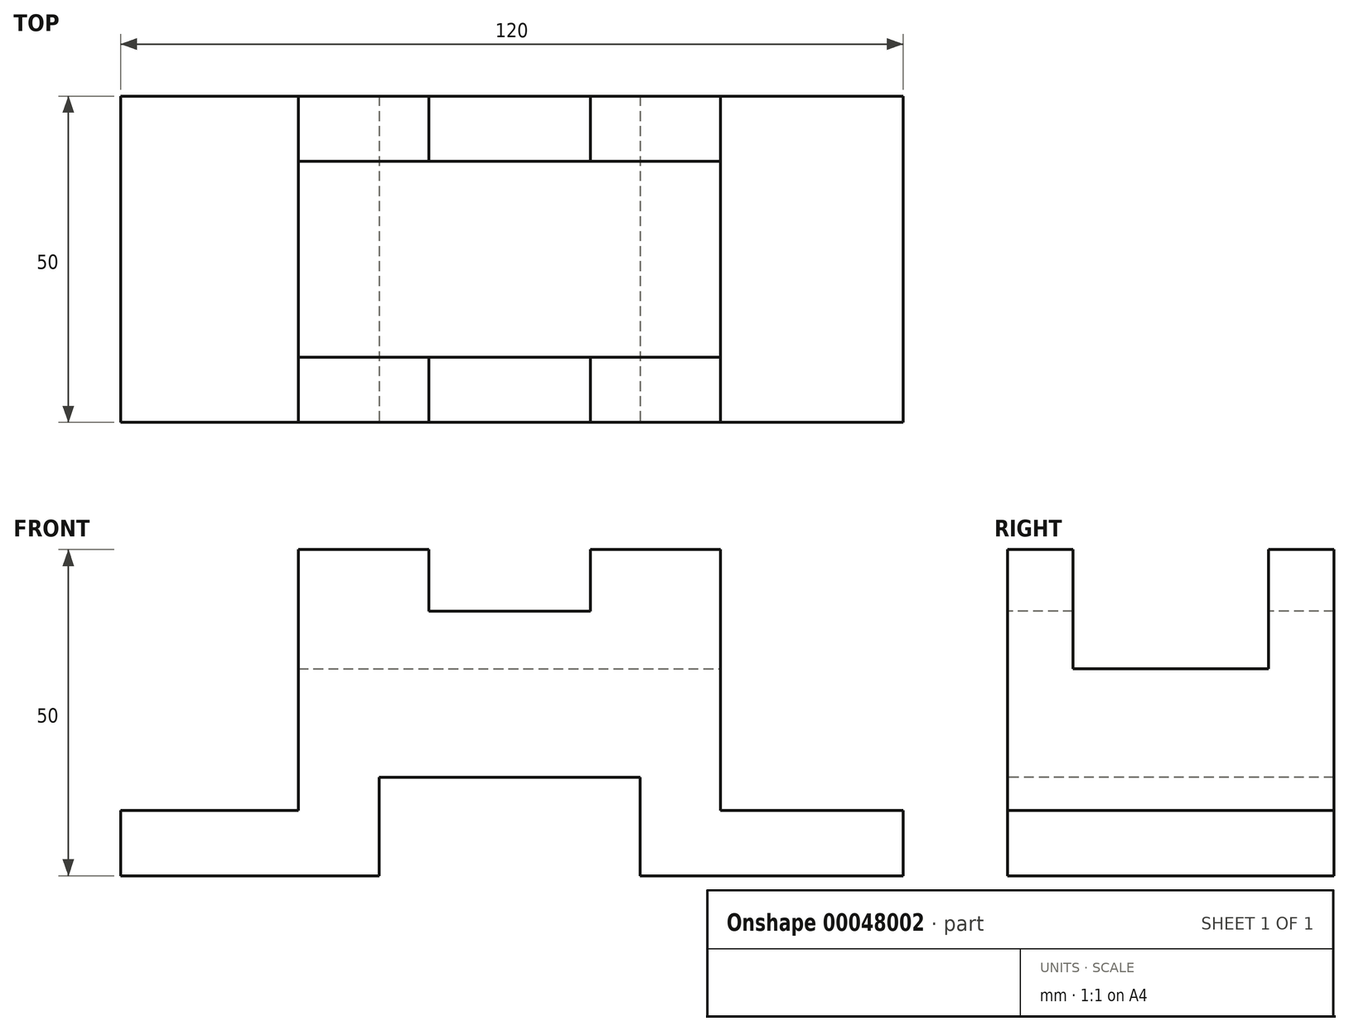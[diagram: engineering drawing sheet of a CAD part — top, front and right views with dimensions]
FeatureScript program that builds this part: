
annotation { "Feature Type Name" : "Feature", "Feature Type Description" : "" }
export const myFeature = defineFeature(function(context is Context, id is Id, definition is map)
    precondition{}
    {
        {
            var Q0;
            Q0=qCreatedBy(makeId("Front.planeOp"),FACE);
            var sketch = newSketch(context, id + "F0", { "sketchPlane" : qUnion([Q0])});
            skLineSegment(sketch, "E0", {"start": v(0, 0) * mm, "end": v(40.36, 0) * mm});
            skLineSegment(sketch, "E1", {"start": v(40.36, 0) * mm, "end": v(40.36, 10) * mm});
            skLineSegment(sketch, "E2", {"start": v(40.36, 10) * mm, "end": v(12.36, 10) * mm});
            skLineSegment(sketch, "E3", {"start": v(12.36, 10) * mm, "end": v(12.36, 50) * mm});
            skLineSegment(sketch, "E4", {"start": v(12.36, 50) * mm, "end": v(-7.64, 50) * mm});
            skLineSegment(sketch, "E5", {"start": v(-7.64, 50) * mm, "end": v(-7.64, 40.55) * mm});
            skLineSegment(sketch, "E6", {"start": v(-7.64, 40.55) * mm, "end": v(-32.36, 40.55) * mm});
            skLineSegment(sketch, "E7", {"start": v(-32.36, 40.55) * mm, "end": v(-32.36, 50) * mm});
            skLineSegment(sketch, "E8", {"start": v(-32.36, 50) * mm, "end": v(-52.36, 50) * mm});
            skLineSegment(sketch, "E9", {"start": v(-52.36, 50) * mm, "end": v(-52.36, 10) * mm});
            skLineSegment(sketch, "E10", {"start": v(-52.36, 10) * mm, "end": v(-79.64, 10) * mm});
            skLineSegment(sketch, "E11", {"start": v(-79.64, 10) * mm, "end": v(-79.64, 0) * mm});
            skLineSegment(sketch, "E12", {"start": v(-79.64, 0) * mm, "end": v(-40, 0) * mm});
            skLineSegment(sketch, "E13", {"start": v(-40, 0) * mm, "end": v(-40, 15.1) * mm});
            skLineSegment(sketch, "E14", {"start": v(-40, 15.1) * mm, "end": v(0, 15.1) * mm});
            skLineSegment(sketch, "E15", {"start": v(0, 15.1) * mm, "end": v(0, 0) * mm});
            skSolve(sketch);
        }
        {
            var Q0;
            Q0=makeQuery(id+"F0.imprint","IMPRINT",FACE,{"disambiguationData":[TD([[makeQuery(id+"F0.imprint","IMPRINT",EDGE,{"derivedFrom":sQuery(id+"F0.wireOp",EDGE,"E0")}),1.0]])]});
            extrude(context, id + "F1", {"entities" : qUnion([Q0]), "oppositeDirection" : true, "depth" : 50 * mm});
        }
        {
            var Q0;
            Q0=makeQuery(id+"F1.opExtrude","SWEPT_FACE",FACE,{"disambiguationData":[OSD([sQuery(id+"F0.wireOp",EDGE,"E3")])]});
            var sketch = newSketch(context, id + "F2", { "sketchPlane" : qUnion([Q0])});
            skLineSegment(sketch, "E16", {"start": v(50, 50) * mm, "end": v(40, 50) * mm});
            skLineSegment(sketch, "E17", {"start": v(40, 50) * mm, "end": v(40, 31.71) * mm});
            skLineSegment(sketch, "E18", {"start": v(40, 31.71) * mm, "end": v(10, 31.71) * mm});
            skLineSegment(sketch, "E19", {"start": v(10, 31.71) * mm, "end": v(10, 50) * mm});
            skSolve(sketch);
        }
        {
            var Q0;
            {var subQ2=sQuery(id+"F2.wireOp",EDGE,"E17");Q0=makeQuery(id+"F2.imprint","IMPRINT",FACE,{"disambiguationData":[TD([[makeQuery(id+"F2.imprint","IMPRINT",EDGE,{"derivedFrom":subQ2}),-1.0]])]});}
            extrude(context, id + "F3", {"entities" : qUnion([Q0]), "operationType" : NewBodyOperationType.REMOVE, "endBound" : BoundingType.THROUGH_ALL, "oppositeDirection" : true, "depth" : 25 * mm});
        }
    });
